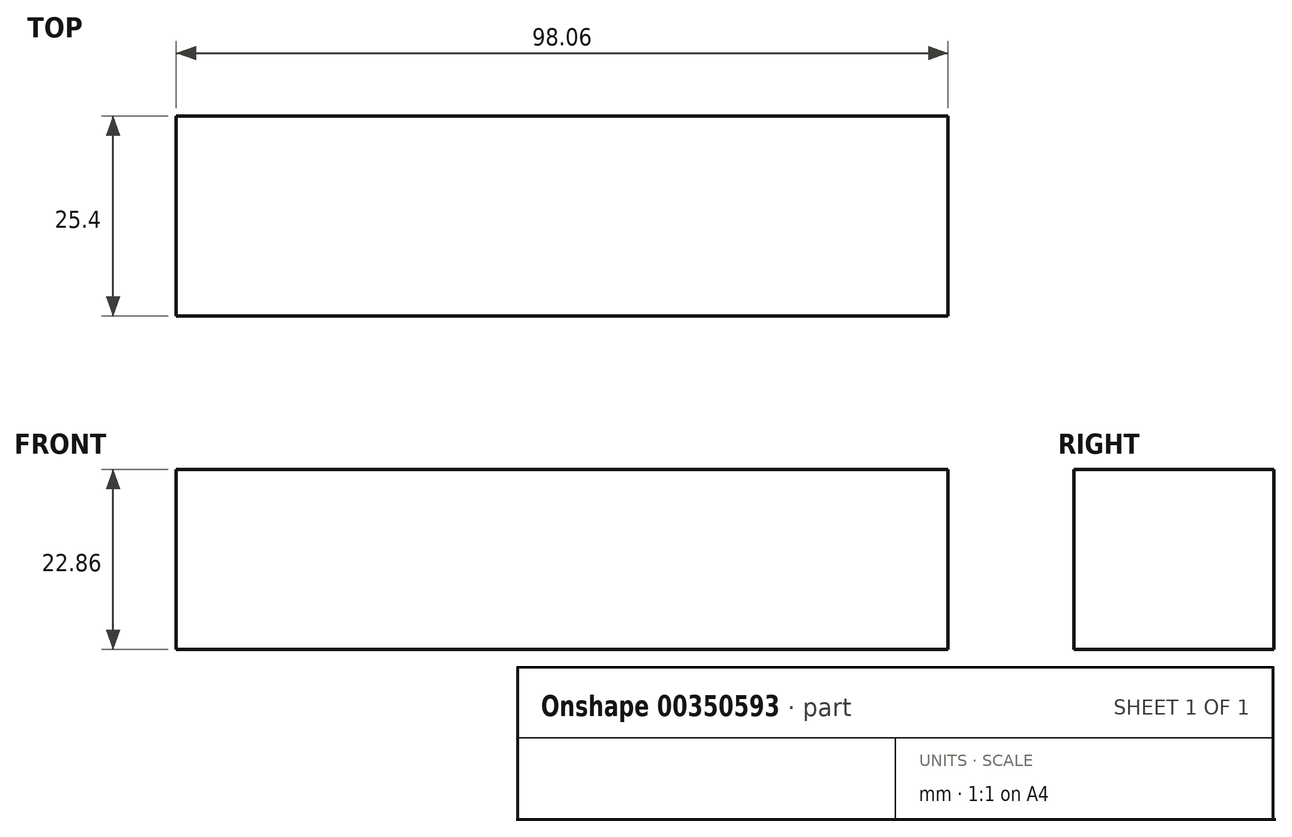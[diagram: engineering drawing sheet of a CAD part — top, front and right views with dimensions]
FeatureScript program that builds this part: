
annotation { "Feature Type Name" : "Feature", "Feature Type Description" : "" }
export const myFeature = defineFeature(function(context is Context, id is Id, definition is map)
    precondition{}
    {
        {
            var Q0;
            Q0=qCreatedBy(makeId("Front.planeOp"),FACE);
            var sketch = newSketch(context, id + "F0", { "sketchPlane" : qUnion([Q0])});
            skLineSegment(sketch, "E0.bottom", {"start": v(49.03, -11.43) * mm, "end": v(-49.03, -11.43) * mm});
            skLineSegment(sketch, "E0.top", {"start": v(49.03, 11.43) * mm, "end": v(-49.03, 11.43) * mm});
            skLineSegment(sketch, "E0.left", {"start": v(49.03, -11.43) * mm, "end": v(49.03, 11.43) * mm});
            skLineSegment(sketch, "E0.right", {"start": v(-49.03, -11.43) * mm, "end": v(-49.03, 11.43) * mm});
            skPoint(sketch, "E0.middle", {"position": v(0, 0) * mm});
            skSolve(sketch);
        }
        {
            var Q0;
            Q0=makeQuery(id+"F0.imprint","IMPRINT",FACE,{"disambiguationData":[TD([[makeQuery(id+"F0.imprint","IMPRINT",EDGE,{"derivedFrom":sQuery(id+"F0.wireOp",EDGE,"E0.bottom")}),-1.0]])]});
            extrude(context, id + "F1", {"entities" : qUnion([Q0]), "depth" : 25.4 * mm});
        }
    });
